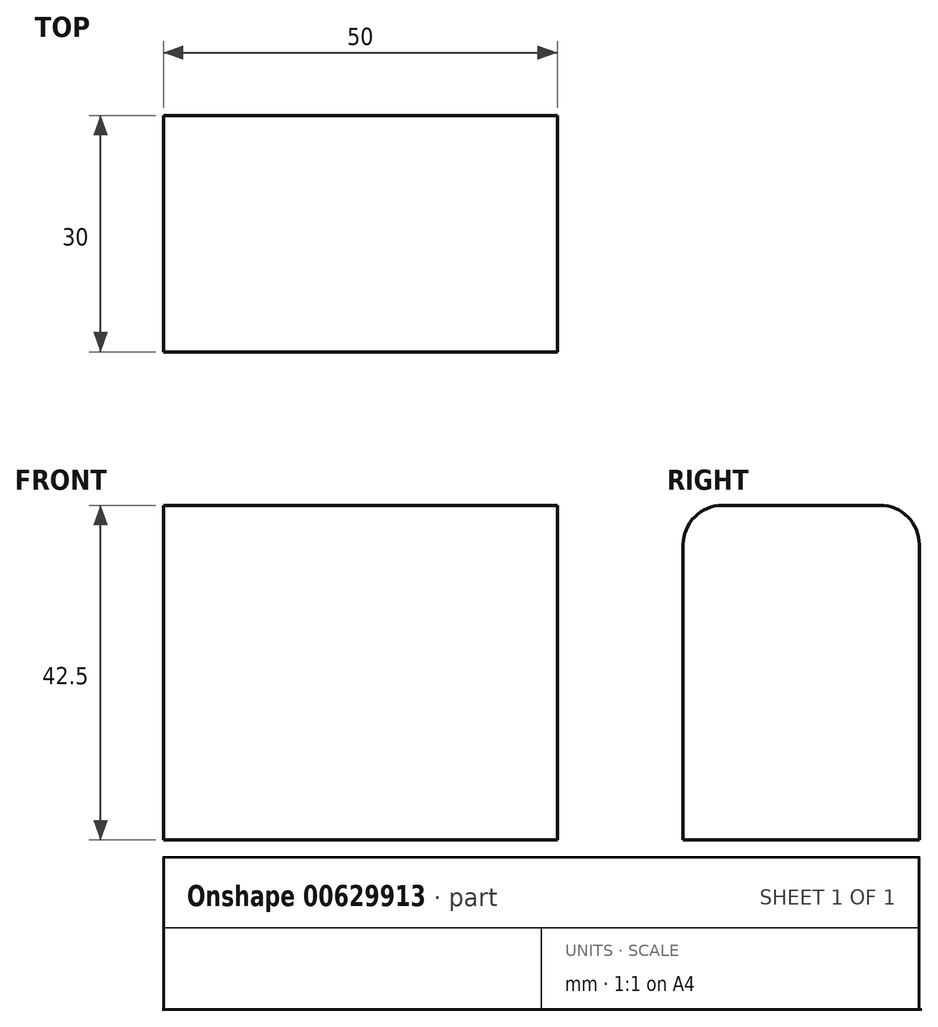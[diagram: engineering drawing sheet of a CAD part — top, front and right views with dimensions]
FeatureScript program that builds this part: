
annotation { "Feature Type Name" : "Feature", "Feature Type Description" : "" }
export const myFeature = defineFeature(function(context is Context, id is Id, definition is map)
    precondition{}
    {
        {
            var Q0;
            Q0=qCreatedBy(makeId("Top.planeOp"),FACE);
            var sketch = newSketch(context, id + "F0", { "sketchPlane" : qUnion([Q0])});
            skLineSegment(sketch, "E0.bottom", {"start": v(0, 0) * mm, "end": v(50, 0) * mm});
            skLineSegment(sketch, "E0.top", {"start": v(0, -30) * mm, "end": v(50, -30) * mm});
            skLineSegment(sketch, "E0.left", {"start": v(0, 0) * mm, "end": v(0, -30) * mm});
            skLineSegment(sketch, "E0.right", {"start": v(50, 0) * mm, "end": v(50, -30) * mm});
            skSolve(sketch);
        }
        {
            var Q0;
            Q0 = qSketchRegion(id + "F0", true);
            extrude(context, id + "F1", {"entities" : qUnion([Q0]), "depth" : 30 * mm, "offsetDistance" : 25 * mm});
        }
        {
            var Q0;
            Q0=makeQuery(id+"F1.opExtrude","CAP_EDGE",EDGE,{"disambiguationData":[OSD([sQuery(id+"F0.wireOp",EDGE,"E0.top")])],"isStart":true});
            var Q1;
            Q1=makeQuery(id+"F1.opExtrude","CAP_EDGE",EDGE,{"disambiguationData":[OSD([sQuery(id+"F0.wireOp",EDGE,"E0.bottom")])],"isStart":true});
            var Q2;
            Q2=makeQuery(id+"F1.opExtrude","CAP_EDGE",EDGE,{"disambiguationData":[OSD([sQuery(id+"F0.wireOp",EDGE,"E0.bottom")])],"isStart":false});
            var Q3;
            Q3=makeQuery(id+"F1.opExtrude","CAP_EDGE",EDGE,{"disambiguationData":[OSD([sQuery(id+"F0.wireOp",EDGE,"E0.top")])],"isStart":false});
            fillet(context, id + "F2", {"entities" : qUnion([Q0, Q1, Q2, Q3]), "radius" : 5 * mm, "tangentPropagation" : true, "allowEdgeOverflow" : false});
        }
        {
            var Q0;
            Q0 = qSketchRegion(id + "F0", true);
            extrude(context, id + "F3", {"entities" : qUnion([Q0]), "operationType" : NewBodyOperationType.ADD, "endBound" : BoundingType.SYMMETRIC, "depth" : 25 * mm, "offsetDistance" : 25 * mm});
        }
    });
